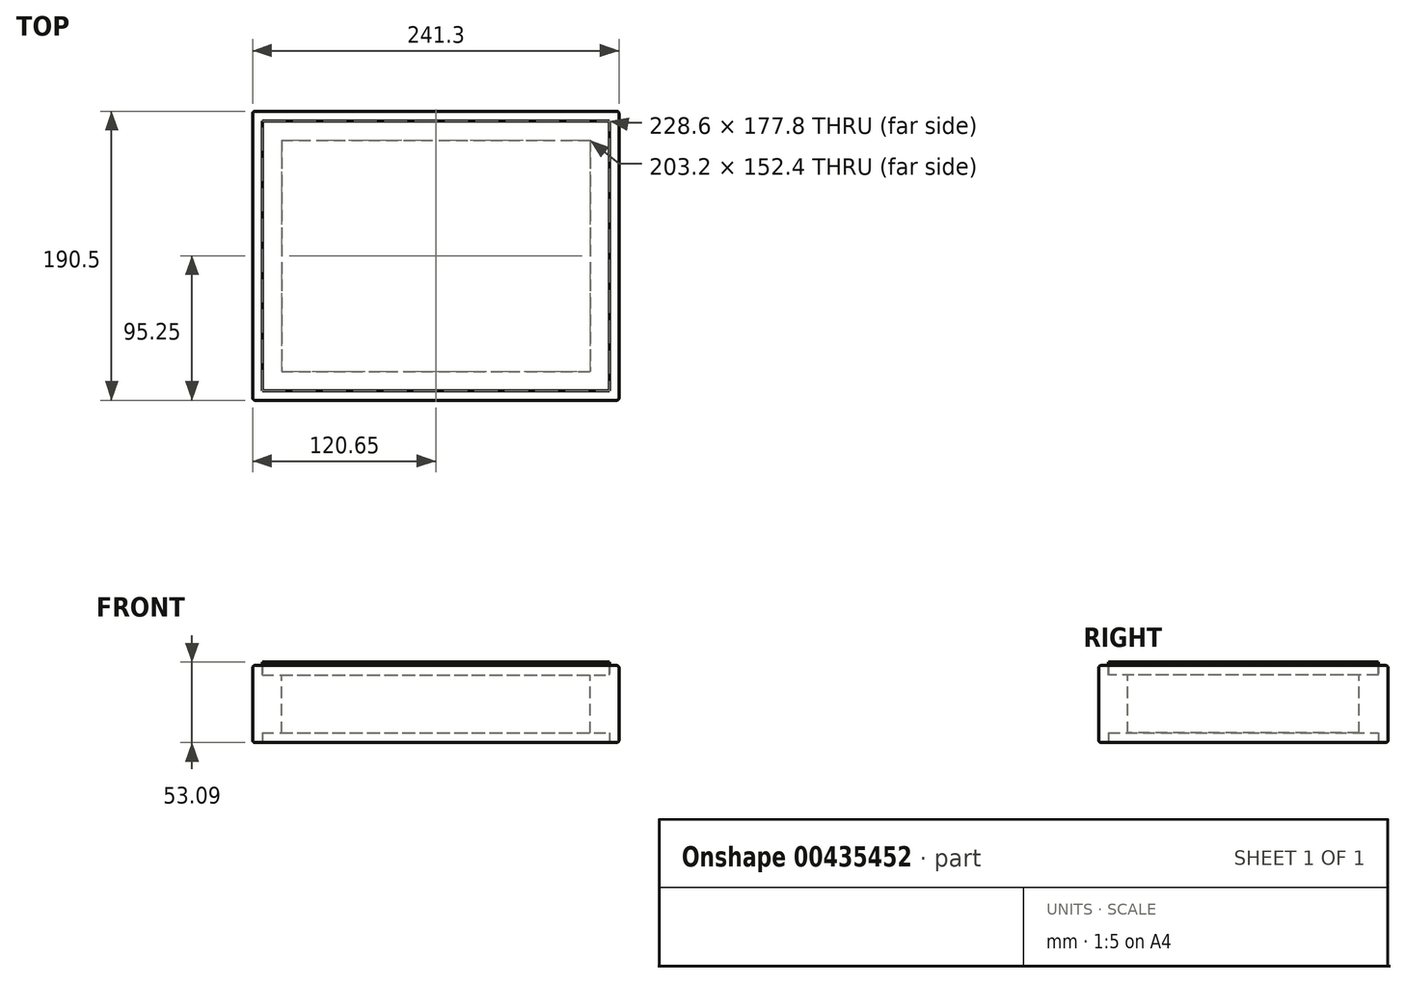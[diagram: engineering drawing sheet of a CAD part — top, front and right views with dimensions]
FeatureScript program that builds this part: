
annotation { "Feature Type Name" : "Feature", "Feature Type Description" : "" }
export const myFeature = defineFeature(function(context is Context, id is Id, definition is map)
    precondition{}
    {
        {
            var Q0;
            Q0=qCreatedBy(makeId("Front.planeOp"),FACE);
            var sketch = newSketch(context, id + "F0", { "sketchPlane" : qUnion([Q0])});
            skLineSegment(sketch, "E0.bottom", {"start": v(0, 0) * mm, "end": v(241.3, 0) * mm});
            skLineSegment(sketch, "E0.top", {"start": v(0, 50.8) * mm, "end": v(241.3, 50.8) * mm});
            skLineSegment(sketch, "E0.left", {"start": v(0, 0) * mm, "end": v(0, 50.8) * mm});
            skLineSegment(sketch, "E0.right", {"start": v(241.3, 0) * mm, "end": v(241.3, 50.8) * mm});
            skSolve(sketch);
        }
        {
            var Q0;
            Q0=makeQuery(id+"F0.imprint","IMPRINT",FACE,{"disambiguationData":[TD([[makeQuery(id+"F0.imprint","IMPRINT",EDGE,{"derivedFrom":sQuery(id+"F0.wireOp",EDGE,"E0.bottom")}),1.0]])]});
            extrude(context, id + "F1", {"entities" : qUnion([Q0]), "oppositeDirection" : true, "depth" : 190.5 * mm});
        }
        {
            var Q0;
            Q0=makeQuery(id+"F1.opExtrude","SWEPT_FACE",FACE,{"disambiguationData":[OSD([sQuery(id+"F0.wireOp",EDGE,"E0.top")])]});
            var sketch = newSketch(context, id + "F2", { "sketchPlane" : qUnion([Q0])});
            skLineSegment(sketch, "E1.bottom", {"start": v(19.05, 171.45) * mm, "end": v(222.25, 171.45) * mm});
            skLineSegment(sketch, "E1.top", {"start": v(19.05, 19.05) * mm, "end": v(222.25, 19.05) * mm});
            skLineSegment(sketch, "E1.left", {"start": v(19.05, 171.45) * mm, "end": v(19.05, 19.05) * mm});
            skLineSegment(sketch, "E1.right", {"start": v(222.25, 171.45) * mm, "end": v(222.25, 19.05) * mm});
            skSolve(sketch);
        }
        {
            var Q0;
            Q0=makeQuery(id+"F2.imprint","IMPRINT",FACE,{"disambiguationData":[TD([[makeQuery(id+"F2.imprint","IMPRINT",EDGE,{"derivedFrom":sQuery(id+"F2.wireOp",EDGE,"E1.bottom")}),-1.0]])]});
            extrude(context, id + "F3", {"entities" : qUnion([Q0]), "operationType" : NewBodyOperationType.REMOVE, "endBound" : BoundingType.UP_TO_NEXT, "oppositeDirection" : true, "depth" : 25.4 * mm});
        }
        {
            var Q0;
            Q0=makeQuery(id+"F1.opExtrude","SWEPT_FACE",FACE,{"disambiguationData":[OSD([sQuery(id+"F0.wireOp",EDGE,"E0.top")])]});
            var sketch = newSketch(context, id + "F4", { "sketchPlane" : qUnion([Q0])});
            skLineSegment(sketch, "E2.bottom", {"start": v(6.35, 184.15) * mm, "end": v(234.95, 184.15) * mm});
            skLineSegment(sketch, "E2.top", {"start": v(6.35, 6.35) * mm, "end": v(234.95, 6.35) * mm});
            skLineSegment(sketch, "E2.left", {"start": v(6.35, 184.15) * mm, "end": v(6.35, 6.35) * mm});
            skLineSegment(sketch, "E2.right", {"start": v(234.95, 184.15) * mm, "end": v(234.95, 6.35) * mm});
            skSolve(sketch);
        }
        {
            var Q0;
            Q0=makeQuery(id+"F4.imprint","IMPRINT",FACE,{"disambiguationData":[TD([[makeQuery(id+"F4.imprint","IMPRINT",EDGE,{"derivedFrom":sQuery(id+"F4.wireOp",EDGE,"E2.bottom")}),-1.0]])]});
            extrude(context, id + "F5", {"entities" : qUnion([Q0]), "operationType" : NewBodyOperationType.REMOVE, "oppositeDirection" : true, "depth" : 6.35 * mm});
        }
        {
            var Q0;
            Q0=makeQuery(id+"F1.opExtrude","SWEPT_FACE",FACE,{"disambiguationData":[OSD([sQuery(id+"F0.wireOp",EDGE,"E0.bottom")])]});
            var sketch = newSketch(context, id + "F6", { "sketchPlane" : qUnion([Q0])});
            skLineSegment(sketch, "E3.bottom", {"start": v(6.35, -6.35) * mm, "end": v(234.95, -6.35) * mm});
            skLineSegment(sketch, "E3.top", {"start": v(6.35, -184.15) * mm, "end": v(234.95, -184.15) * mm});
            skLineSegment(sketch, "E3.left", {"start": v(6.35, -6.35) * mm, "end": v(6.35, -184.15) * mm});
            skLineSegment(sketch, "E3.right", {"start": v(234.95, -6.35) * mm, "end": v(234.95, -184.15) * mm});
            skSolve(sketch);
        }
        {
            var Q0;
            Q0=makeQuery(id+"F6.imprint","IMPRINT",FACE,{"disambiguationData":[TD([[makeQuery(id+"F6.imprint","IMPRINT",EDGE,{"derivedFrom":sQuery(id+"F6.wireOp",EDGE,"E3.bottom")}),-1.0]])]});
            extrude(context, id + "F7", {"entities" : qUnion([Q0]), "operationType" : NewBodyOperationType.REMOVE, "oppositeDirection" : true, "depth" : 6.35 * mm});
        }
        {
            var Q0;
            Q0=makeQuery(id+"F1.opExtrude","CAP_EDGE",EDGE,{"disambiguationData":[OSD([sQuery(id+"F0.wireOp",EDGE,"E0.top")])],"isStart":true});
            var Q1;
            Q1=makeQuery(id+"F1.opExtrude","CAP_EDGE",EDGE,{"disambiguationData":[OSD([sQuery(id+"F0.wireOp",EDGE,"E0.left")])],"isStart":true});
            var Q2;
            Q2=makeQuery(id+"F1.opExtrude","SWEPT_EDGE",EDGE,{"disambiguationData":[OSD([sQuery(id+"F0.wireOp",EDGE,"E0.top"),sQuery(id+"F0.wireOp",EDGE,"E0.left")])]});
            var Q3;
            Q3=makeQuery(id+"F1.opExtrude","CAP_EDGE",EDGE,{"disambiguationData":[OSD([sQuery(id+"F0.wireOp",EDGE,"E0.right")])],"isStart":true});
            var Q4;
            Q4=makeQuery(id+"F1.opExtrude","SWEPT_EDGE",EDGE,{"disambiguationData":[OSD([sQuery(id+"F0.wireOp",EDGE,"E0.top"),sQuery(id+"F0.wireOp",EDGE,"E0.right")])]});
            var Q5;
            Q5=makeQuery(id+"F1.opExtrude","CAP_EDGE",EDGE,{"disambiguationData":[OSD([sQuery(id+"F0.wireOp",EDGE,"E0.top")])],"isStart":false});
            var Q6;
            Q6=makeQuery(id+"F1.opExtrude","CAP_EDGE",EDGE,{"disambiguationData":[OSD([sQuery(id+"F0.wireOp",EDGE,"E0.right")])],"isStart":false});
            var Q7;
            Q7=makeQuery(id+"F1.opExtrude","CAP_EDGE",EDGE,{"disambiguationData":[OSD([sQuery(id+"F0.wireOp",EDGE,"E0.left")])],"isStart":false});
            var Q8;
            Q8=makeQuery(id+"F1.opExtrude","CAP_EDGE",EDGE,{"disambiguationData":[OSD([sQuery(id+"F0.wireOp",EDGE,"E0.bottom")])],"isStart":false});
            var Q9;
            Q9=makeQuery(id+"F1.opExtrude","SWEPT_EDGE",EDGE,{"disambiguationData":[OSD([sQuery(id+"F0.wireOp",EDGE,"E0.bottom"),sQuery(id+"F0.wireOp",EDGE,"E0.left")])]});
            var Q10;
            Q10=makeQuery(id+"F1.opExtrude","CAP_EDGE",EDGE,{"disambiguationData":[OSD([sQuery(id+"F0.wireOp",EDGE,"E0.bottom")])],"isStart":true});
            var Q11;
            Q11=makeQuery(id+"F1.opExtrude","SWEPT_EDGE",EDGE,{"disambiguationData":[OSD([sQuery(id+"F0.wireOp",EDGE,"E0.bottom"),sQuery(id+"F0.wireOp",EDGE,"E0.right")])]});
            fillet(context, id + "F8", {"entities" : qUnion([Q0, Q1, Q2, Q3, Q4, Q5, Q6, Q7, Q8, Q9, Q10, Q11]), "radius" : 1.59 * mm, "tangentPropagation" : true, "allowEdgeOverflow" : false});
        }
        {
            var Q0;
            Q0=makeQuery(id+"F5.boolean.opBoolean","COPY",FACE,{"derivedFrom":makeQuery(id+"F5.opExtrude","CAP_FACE",FACE,{"disambiguationData":[OSD([sQuery(id+"F2.wireOp",EDGE,"E1.bottom"),sQuery(id+"F2.wireOp",EDGE,"E1.top"),sQuery(id+"F2.wireOp",EDGE,"E1.left"),sQuery(id+"F2.wireOp",EDGE,"E1.right"),sQuery(id+"F4.wireOp",EDGE,"E2.bottom"),sQuery(id+"F4.wireOp",EDGE,"E2.top"),sQuery(id+"F4.wireOp",EDGE,"E2.left"),sQuery(id+"F4.wireOp",EDGE,"E2.right")])],"isStart":false})});
            var sketch = newSketch(context, id + "F9", { "sketchPlane" : qUnion([Q0])});
            skLineSegment(sketch, "E4.bottom", {"start": v(6.35, 184.15) * mm, "end": v(234.95, 184.15) * mm});
            skLineSegment(sketch, "E4.top", {"start": v(6.35, 6.35) * mm, "end": v(234.95, 6.35) * mm});
            skLineSegment(sketch, "E4.left", {"start": v(6.35, 184.15) * mm, "end": v(6.35, 6.35) * mm});
            skLineSegment(sketch, "E4.right", {"start": v(234.95, 184.15) * mm, "end": v(234.95, 6.35) * mm});
            skSolve(sketch);
        }
        {
            var Q0;
            Q0 = qSketchRegion(id + "F9", true);
            extrude(context, id + "F10", {"entities" : qUnion([Q0]), "depth" : 8.64 * mm});
        }
    });
